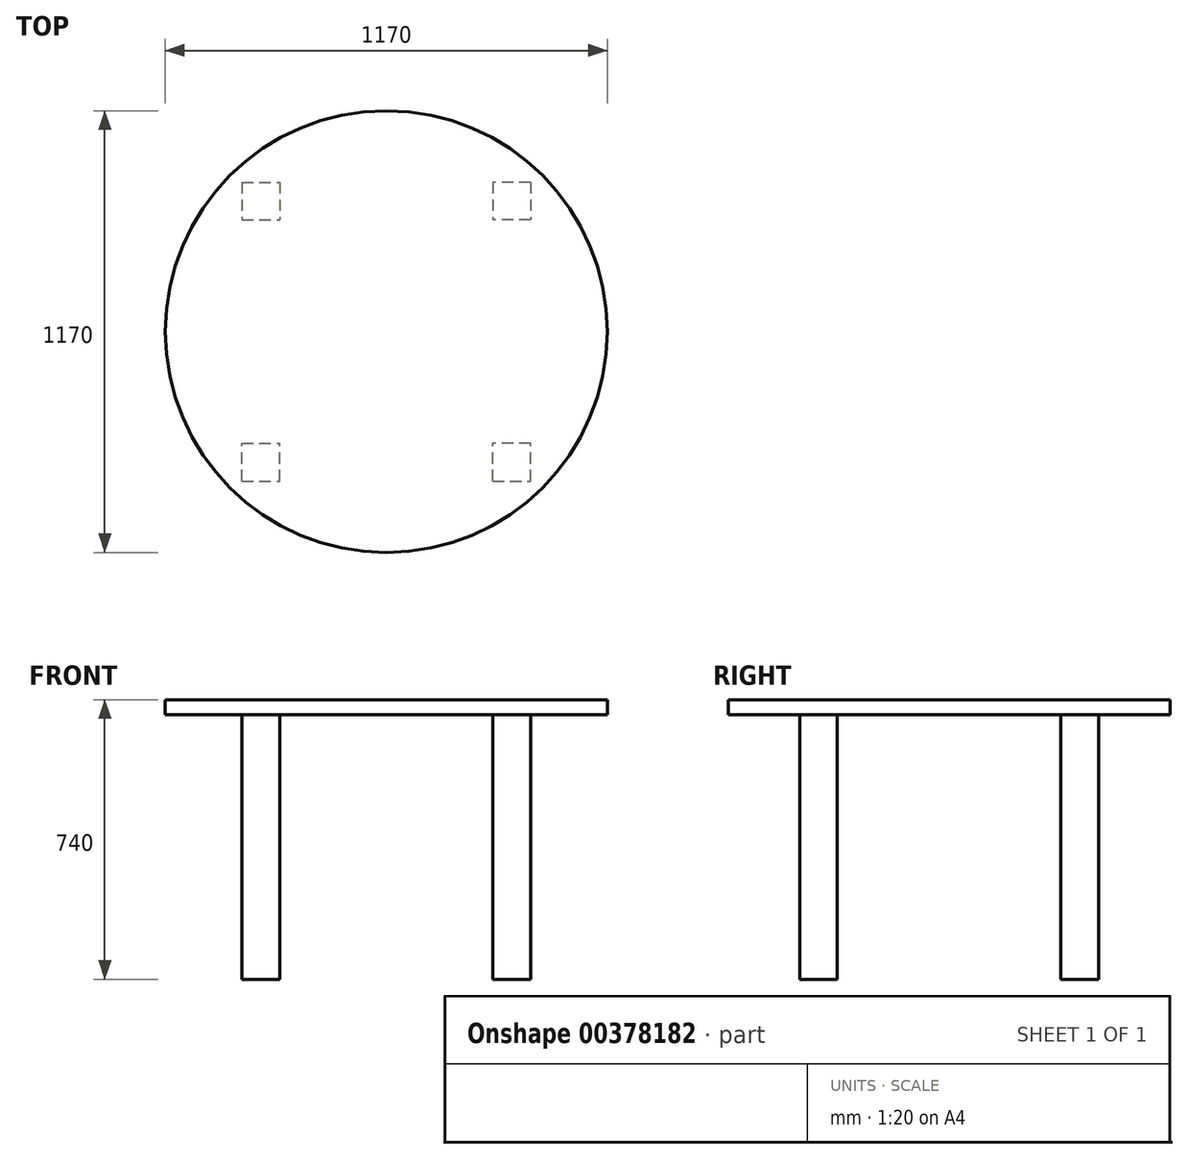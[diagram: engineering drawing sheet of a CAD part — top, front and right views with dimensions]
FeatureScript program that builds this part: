
annotation { "Feature Type Name" : "Feature", "Feature Type Description" : "" }
export const myFeature = defineFeature(function(context is Context, id is Id, definition is map)
    precondition{}
    {
        {
            var Q0;
            Q0=qCreatedBy(makeId("Top.planeOp"),FACE);
            var sketch = newSketch(context, id + "F0", { "sketchPlane" : qUnion([Q0])});
            skCircle(sketch, "E0", {"center": v(0, 0) * mm, "radius": 585 * mm});
            skSolve(sketch);
        }
        {
            var Q0;
            Q0 = qSketchRegion(id + "F0", true);
            extrude(context, id + "F1", {"entities" : qUnion([Q0]), "oppositeDirection" : true, "depth" : 40 * mm});
        }
        {
            var Q0;
            Q0=makeQuery(id+"F1.opExtrude","CAP_FACE",FACE,{"disambiguationData":[OSD([sQuery(id+"F0.wireOp",EDGE,"E0")])],"isStart":false});
            var sketch = newSketch(context, id + "F2", { "sketchPlane" : qUnion([Q0])});
            skCircle(sketch, "E1", {"center": v(0, 0) * mm, "radius": 550 * mm, "construction": true});
            skLineSegment(sketch, "E2.bottom", {"start": v(-381.93, 395.77) * mm, "end": v(-281.93, 395.77) * mm});
            skLineSegment(sketch, "E2.top", {"start": v(-381.93, 295.77) * mm, "end": v(-281.93, 295.77) * mm});
            skLineSegment(sketch, "E2.left", {"start": v(-381.93, 395.77) * mm, "end": v(-381.93, 295.77) * mm});
            skLineSegment(sketch, "E2.right", {"start": v(-281.93, 395.77) * mm, "end": v(-281.93, 295.77) * mm});
            skCircle(sketch, "E3", {"center": v(0, 0) * mm, "radius": 408.6 * mm, "construction": true});
            skLineSegment(sketch, "E4", {"start": v(-381.93, 395.77) * mm, "end": v(381.93, 395.77) * mm});
            skLineSegment(sketch, "E5", {"start": v(381.93, 395.77) * mm, "end": v(-381.93, 395.77) * mm, "construction": true});
            skLineSegment(sketch, "E6", {"start": v(-381.93, 395.77) * mm, "end": v(-381.93, -395.77) * mm, "construction": true});
            skLineSegment(sketch, "E7", {"start": v(-381.93, -395.77) * mm, "end": v(381.93, -395.77) * mm, "construction": true});
            skLineSegment(sketch, "E8", {"start": v(381.93, -395.77) * mm, "end": v(381.93, 395.77) * mm, "construction": true});
            skLineSegment(sketch, "E9.bottom", {"start": v(381.93, 395.77) * mm, "end": v(281.93, 395.77) * mm});
            skLineSegment(sketch, "E9.top", {"start": v(381.93, 295.77) * mm, "end": v(281.93, 295.77) * mm});
            skLineSegment(sketch, "E9.left", {"start": v(381.93, 395.77) * mm, "end": v(381.93, 295.77) * mm});
            skLineSegment(sketch, "E9.right", {"start": v(281.93, 395.77) * mm, "end": v(281.93, 295.77) * mm});
            skLineSegment(sketch, "E10.bottom", {"start": v(381.93, -395.77) * mm, "end": v(281.93, -395.77) * mm});
            skLineSegment(sketch, "E10.top", {"start": v(381.93, -295.77) * mm, "end": v(281.93, -295.77) * mm});
            skLineSegment(sketch, "E10.left", {"start": v(381.93, -395.77) * mm, "end": v(381.93, -295.77) * mm});
            skLineSegment(sketch, "E10.right", {"start": v(281.93, -395.77) * mm, "end": v(281.93, -295.77) * mm});
            skLineSegment(sketch, "E11.bottom", {"start": v(-381.93, -395.77) * mm, "end": v(-281.93, -395.77) * mm});
            skLineSegment(sketch, "E11.top", {"start": v(-381.93, -295.77) * mm, "end": v(-281.93, -295.77) * mm});
            skLineSegment(sketch, "E11.left", {"start": v(-381.93, -395.77) * mm, "end": v(-381.93, -295.77) * mm});
            skLineSegment(sketch, "E11.right", {"start": v(-281.93, -395.77) * mm, "end": v(-281.93, -295.77) * mm});
            skSolve(sketch);
        }
        {
            var Q0;
            Q0 = qSketchRegion(id + "F2", true);
            extrude(context, id + "F3", {"entities" : qUnion([Q0]), "operationType" : NewBodyOperationType.ADD, "depth" : 700 * mm});
        }
    });
